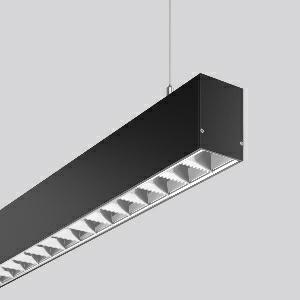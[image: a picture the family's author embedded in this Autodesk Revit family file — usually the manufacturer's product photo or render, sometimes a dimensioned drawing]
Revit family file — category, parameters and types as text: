
# Revit family: less_is_more_50_312337_003_1_6295
name_source: partatom
category: Lighting Fixtures
units: mm (PartAtom-declared; Revit-internal decimal feet)

## family parameters
Cut with Voids When Loaded = No
Host = Face
Light Source = No
Part Type = Normal
Room Calculation Point = No
Round Connector Dimension = Use Diameter
Shared = No

## types (1)
- LESS IS MORE 50 (1 x LED Modul 840, 4450 lm, 4000)
    Apparent Load = 35 VA
    CIE Flux Codes = 95 100 100 100 100
    Color Rendering = 80
    Color Temperature = 4000
    Default Elevation = 1800 mm
    Description = Series: LESS IS MORE 50
Linear pendant luminaire for aesthetically sophisticated lighting. Housing: extruded aluminium profile, powder-coated. End cap aluminium powder-coated. Canopy made of aluminium, powder-coated. Alea optical system: Reflector structure (ABS, Aluminium-coated, highly polished) with integrated diffuser made of non-yellowing plastic (PMMA) opal for glare-free light at the workstation (screen-compliant according to EN 12464-1). Direct light emission. Suitable for pendant. 2-point steel cable suspension freely positionable and infinitely height-adjustable. Special lengths available on request. LED unit with integrated converter interchangeable and removable. Suitable for through-wiring. With sensors or as a safety luminaire on request. 
Colour: deep black, matt (RAL 9005)
Length: 1407 mm
Width: 57 mm
Height: 75 mm
Suspension length: 2000 mm
Lamp: LED
Socket: without socket
Colour temperature: 4000K
Colour rendering index (CRI): 80
System power: 35 W
Rated luminous flux: 4450 lm
Luminous efficiency: 127 lm/W
Control gear: Regulated power supply
Protection class: I
Type of protection: IP 20
    Height = 75 mm
    Lamp = 1 x LED Modul 840
    Lamp Light Flux = 4450 lm
    Lamp count = 1
    Length = 1407 mm
    Lifetime = 50000 h
    Luminous efficacy = 127 lm/W
    Manufacturer = RZB
    ModVariant = No
    Model = 312337.003.1
    Mounting Place = Ceiling
    Mounting Type = Pendant
    Number of Poles = 1
    OnlyDefault = Yes
    Power Factor = 1
    Product Name = LESS IS MORE 50
    Product group = Pendant LED linear luminaires
    ProductGroupID = 907
    Protection Class = Protection class I
    Protection Degree = IP 20
    RLX_Detail_Level = 1
    RLX_Emergency_Light_Flux = 0 lm
    RLX_Emergency_Type = 0
    RLX_Emergency_Type_DB = No
    RlxData = <blob elided: 39597 chars, md5=a651d52d>
    Socket = socket
    Standby Power = 0 W
    System Light Flux = 4450 lm
    System Power = 35 W
    Type Comments = Product without accessories
    Type Image = 312342.003.jpg
    URL = http://relux.com
    VarID = ---
    Voltage = 230 V
    Voltage Range = 220-240 V
    Weight = 0.00 kg
    Width = 57 mm

## geometry (parser evidence)
native form markers: Blend x4, Sweep x9
no freeform markers — native parametric forms only
